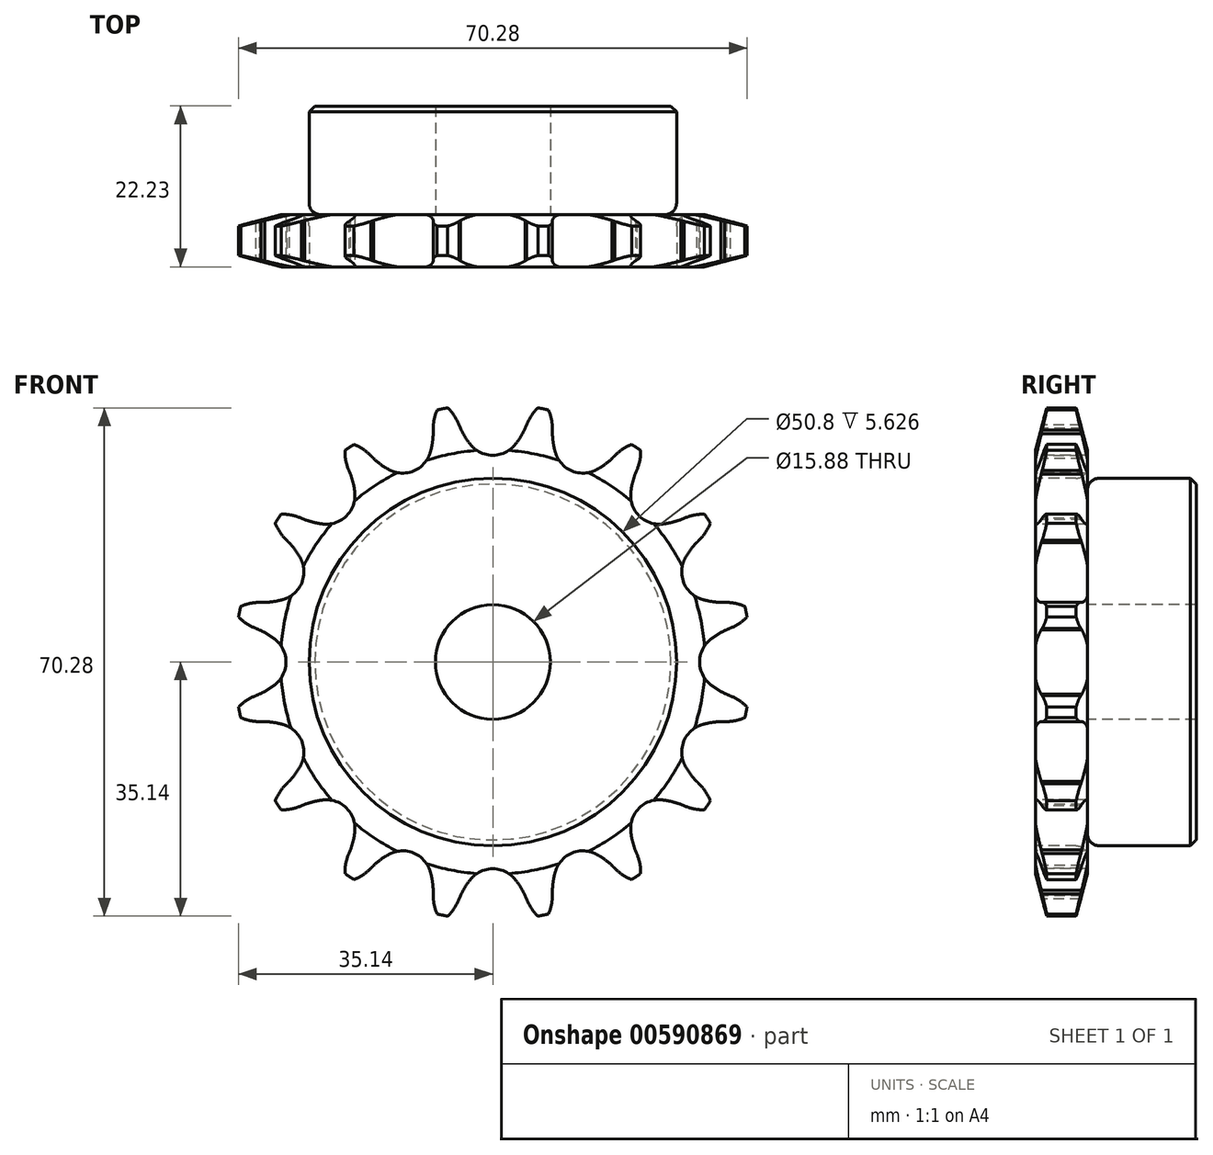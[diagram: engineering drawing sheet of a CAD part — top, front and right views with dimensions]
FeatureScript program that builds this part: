
annotation { "Feature Type Name" : "Feature", "Feature Type Description" : "" }
export const myFeature = defineFeature(function(context is Context, id is Id, definition is map)
    precondition{}
    {
        {
            var Q0;
            Q0=qCreatedBy(makeId("Right.planeOp"),FACE);
            var sketch = newSketch(context, id + "F0", { "sketchPlane" : qUnion([Q0])});
            skLineSegment(sketch, "E0", {"start": v(0, 0) * mm, "end": v(16.36, 0) * mm, "construction": true});
            skLineSegment(sketch, "E1.bottom", {"start": v(0, 7.94) * mm, "end": v(7.21, 7.94) * mm});
            skLineSegment(sketch, "E1.top", {"start": v(0, 35.69) * mm, "end": v(7.21, 35.69) * mm});
            skLineSegment(sketch, "E1.left", {"start": v(0, 7.94) * mm, "end": v(0, 35.69) * mm});
            skLineSegment(sketch, "E1.right", {"start": v(7.21, 7.94) * mm, "end": v(7.21, 35.69) * mm});
            skLineSegment(sketch, "E2.bottom", {"start": v(0, 7.94) * mm, "end": v(22.23, 7.94) * mm});
            skLineSegment(sketch, "E2.top", {"start": v(0, 25.4) * mm, "end": v(22.23, 25.4) * mm});
            skLineSegment(sketch, "E2.left", {"start": v(0, 7.94) * mm, "end": v(0, 25.4) * mm});
            skLineSegment(sketch, "E2.right", {"start": v(22.23, 7.94) * mm, "end": v(22.22, 25.4) * mm});
            skLineSegment(sketch, "E3.MirrorCS", {"start": v(0, -7.94) * mm, "end": v(7.21, -7.94) * mm});
            skLineSegment(sketch, "E4.MirrorCS", {"start": v(22.23, -7.94) * mm, "end": v(22.23, -25.4) * mm});
            skLineSegment(sketch, "E5.MirrorCS", {"start": v(0, -7.94) * mm, "end": v(0, -25.4) * mm});
            skLineSegment(sketch, "E6.MirrorCS", {"start": v(0, -35.69) * mm, "end": v(7.21, -35.69) * mm});
            skLineSegment(sketch, "E7.MirrorCS", {"start": v(0, -7.94) * mm, "end": v(0, -35.69) * mm});
            skLineSegment(sketch, "E8.MirrorCS", {"start": v(7.21, -7.94) * mm, "end": v(7.21, -35.69) * mm});
            skLineSegment(sketch, "E9.MirrorCS", {"start": v(0, -7.94) * mm, "end": v(22.23, -7.94) * mm});
            skLineSegment(sketch, "E10.MirrorCS", {"start": v(0, -25.4) * mm, "end": v(22.23, -25.4) * mm});
            skSolve(sketch);
        }
        {
            var Q0;
            {var subQ5=sQuery(id+"F0.wireOp",EDGE,"E2.right");Q0=makeQuery(id+"F0.imprint","IMPRINT",FACE,{"disambiguationData":[TD([[makeQuery(id+"F0.imprint","IMPRINT",EDGE,{"derivedFrom":subQ5}),1.0]])]});}
            var Q1;
            {var subQ5=sQuery(id+"F0.wireOp",EDGE,"E2.left");Q1=makeQuery(id+"F0.imprint","IMPRINT",FACE,{"disambiguationData":[TD([[makeQuery(id+"F0.imprint","IMPRINT",EDGE,{"derivedFrom":subQ5}),-1.0]])]});}
            var Q2;
            {var subQ0=sQuery(id+"F0.wireOp",EDGE,"E1.top");Q2=makeQuery(id+"F0.imprint","IMPRINT",FACE,{"disambiguationData":[TD([[makeQuery(id+"F0.imprint","IMPRINT",EDGE,{"derivedFrom":subQ0}),-1.0]])]});}
            var Q3;
            Q3=sQuery(id+"F0.wireOp",EDGE,"E0");
            revolve(context, id + "F1", {"entities" : qUnion([Q0, Q1, Q2]), "axis" : qUnion([Q3]), "revolveType" : RevolveType.FULL});
        }
        {
            var Q0;
            Q0=makeQuery(id+"F1.opRevolve","SWEPT_EDGE",EDGE,{"disambiguationData":[OSD([sQuery(id+"F0.wireOp",EDGE,"E1.right"),sQuery(id+"F0.wireOp",EDGE,"E2.top")])]});
            fillet(context, id + "F2", {"entities" : qUnion([Q0]), "radius" : 1.59 * mm, "tangentPropagation" : true, "allowEdgeOverflow" : false});
        }
        {
            var Q0;
            Q0=makeQuery(id+"F1.opRevolve","SWEPT_EDGE",EDGE,{"disambiguationData":[OSD([sQuery(id+"F0.wireOp",EDGE,"E2.top"),sQuery(id+"F0.wireOp",EDGE,"E2.right")])]});
            chamfer(context, id + "F3", {"entities" : qUnion([Q0]), "width" : 0.8 * mm, "tangentPropagation" : true});
        }
        {
            var Q0;
            Q0=makeQuery(id+"F1.opRevolve","SWEPT_EDGE",EDGE,{"disambiguationData":[OSD([sQuery(id+"F0.wireOp",EDGE,"E1.top"),sQuery(id+"F0.wireOp",EDGE,"E1.left")])]});
            var Q1;
            Q1=makeQuery(id+"F1.opRevolve","SWEPT_EDGE",EDGE,{"disambiguationData":[OSD([sQuery(id+"F0.wireOp",EDGE,"E1.top"),sQuery(id+"F0.wireOp",EDGE,"E1.right")])]});
            chamfer(context, id + "F4", {"entities" : qUnion([Q0, Q1]), "chamferType" : ChamferType.TWO_OFFSETS, "width1" : 6.35 * mm, "oppositeDirection" : false, "width2" : 1.57 * mm, "tangentPropagation" : true});
        }
        {
            var Q0;
            Q0=makeQuery(id+"F1.opRevolve","SWEPT_FACE",FACE,{"disambiguationData":[OSD([sQuery(id+"F0.wireOp",EDGE,"E1.left"),sQuery(id+"F0.wireOp",EDGE,"E2.left")])]});
            var sketch = newSketch(context, id + "F5", { "sketchPlane" : qUnion([Q0])});
            skCircle(sketch, "E11", {"center": v(0, 0) * mm, "radius": 32.55 * mm, "construction": true});
            skLineSegment(sketch, "E12", {"start": v(0, 0) * mm, "end": v(0, 32.55) * mm, "construction": true});
            skLineSegment(sketch, "E13", {"start": v(0, 32.55) * mm, "end": v(42.53, 32.55) * mm, "construction": true});
            skLineSegment(sketch, "E14", {"start": v(0, 32.55) * mm, "end": v(5, 36.56) * mm, "construction": true});
            skLineSegment(sketch, "E15", {"start": v(5, 36.56) * mm, "end": v(-4.46, 32.3) * mm, "construction": true});
            skLineSegment(sketch, "E16", {"start": v(0, 0) * mm, "end": v(-7.13, 35.87) * mm, "construction": true});
            skArc(sketch, "E17", {"start": v(-7.13, 35.87) * mm, "mid": v(-15.95, 26.27) * mm, "end": v(-4.65, 32.77) * mm, "construction": true});
            skArc(sketch, "E18", {"start": v(-4.65, 32.77) * mm, "mid": v(-5.66, 34.5) * mm, "end": v(-7.13, 35.87) * mm});
            skCircle(sketch, "E19.MirrorC", {"center": v(-5, 36.56) * mm, "radius": 10.36 * mm, "construction": true});
            skArc(sketch, "E20.MirrorCS", {"start": v(7.13, 35.87) * mm, "mid": v(15.95, 26.27) * mm, "end": v(4.65, 32.77) * mm, "construction": true});
            skLineSegment(sketch, "E21", {"start": v(-4.65, 32.77) * mm, "end": v(-4.65, 32.77) * mm});
            skLineSegment(sketch, "E22", {"start": v(-4.65, 32.77) * mm, "end": v(-6.37, 36.55) * mm, "construction": true});
            skArc(sketch, "E23", {"start": v(-4.46, 32.3) * mm, "mid": v(-3.84, 31.14) * mm, "end": v(-3.1, 30.07) * mm});
            skArc(sketch, "E24", {"start": v(-3.1, 30.07) * mm, "mid": v(13.83, 41.97) * mm, "end": v(-4.46, 32.3) * mm, "construction": true});
            skArc(sketch, "E25.MirrorCS", {"start": v(4.46, 32.3) * mm, "mid": v(3.84, 31.14) * mm, "end": v(3.1, 30.07) * mm});
            skLineSegment(sketch, "E26.MirrorCS", {"start": v(4.46, 32.3) * mm, "end": v(4.65, 32.77) * mm});
            skArc(sketch, "E27.MirrorCS", {"start": v(4.65, 32.77) * mm, "mid": v(5.66, 34.5) * mm, "end": v(7.13, 35.87) * mm});
            skLineSegment(sketch, "E28", {"start": v(-3.1, 30.07) * mm, "end": v(-3.1, 30.07) * mm});
            skArc(sketch, "E29", {"start": v(-3.1, 30.07) * mm, "mid": v(0, 28.59) * mm, "end": v(3.1, 30.07) * mm});
            skArc(sketch, "E30", {"start": v(3.1, 30.07) * mm, "mid": v(0, 36.51) * mm, "end": v(-3.1, 30.07) * mm, "construction": true});
            skLineSegment(sketch, "E31", {"start": v(-4.65, 32.77) * mm, "end": v(-4.46, 32.3) * mm});
            skArc(sketch, "E32.1.0", {"start": v(-16.84, 28.5) * mm, "mid": v(-18.43, 29.72) * mm, "end": v(-20.32, 30.4) * mm});
            skLineSegment(sketch, "E32.1.1", {"start": v(-16.84, 28.5) * mm, "end": v(-16.48, 28.14) * mm});
            skArc(sketch, "E32.1.2", {"start": v(-16.48, 28.14) * mm, "mid": v(-15.47, 27.3) * mm, "end": v(-14.36, 26.6) * mm});
            skArc(sketch, "E32.1.3", {"start": v(-14.36, 26.6) * mm, "mid": v(-10.94, 26.41) * mm, "end": v(-8.65, 28.96) * mm});
            skArc(sketch, "E32.1.4", {"start": v(-8.24, 31.55) * mm, "mid": v(-8.37, 30.24) * mm, "end": v(-8.65, 28.96) * mm});
            skLineSegment(sketch, "E32.1.5", {"start": v(-8.24, 31.55) * mm, "end": v(-8.24, 32.06) * mm});
            skArc(sketch, "E32.1.6", {"start": v(-8.24, 32.06) * mm, "mid": v(-7.98, 34.05) * mm, "end": v(-7.13, 35.87) * mm});
            skArc(sketch, "E32.2.0", {"start": v(-26.46, 19.88) * mm, "mid": v(-28.4, 20.4) * mm, "end": v(-30.4, 20.32) * mm});
            skLineSegment(sketch, "E32.2.1", {"start": v(-26.46, 19.88) * mm, "end": v(-26, 19.69) * mm});
            skArc(sketch, "E32.2.2", {"start": v(-26, 19.69) * mm, "mid": v(-24.74, 19.3) * mm, "end": v(-23.45, 19.08) * mm});
            skArc(sketch, "E32.2.3", {"start": v(-23.45, 19.08) * mm, "mid": v(-20.21, 20.21) * mm, "end": v(-19.08, 23.45) * mm});
            skArc(sketch, "E32.2.4", {"start": v(-19.69, 26) * mm, "mid": v(-19.3, 24.74) * mm, "end": v(-19.08, 23.45) * mm});
            skLineSegment(sketch, "E32.2.5", {"start": v(-19.69, 26) * mm, "end": v(-19.88, 26.46) * mm});
            skArc(sketch, "E32.2.6", {"start": v(-19.88, 26.46) * mm, "mid": v(-20.4, 28.4) * mm, "end": v(-20.32, 30.4) * mm});
            skArc(sketch, "E33.1.3.0", {"start": v(-32.06, 8.24) * mm, "mid": v(-34.05, 7.98) * mm, "end": v(-35.87, 7.13) * mm});
            skLineSegment(sketch, "E33.4.3.0", {"start": v(-32.06, 8.24) * mm, "end": v(-31.55, 8.24) * mm});
            skArc(sketch, "E33.7.3.0", {"start": v(-31.55, 8.24) * mm, "mid": v(-30.24, 8.37) * mm, "end": v(-28.96, 8.65) * mm});
            skArc(sketch, "E33.11.3.0", {"start": v(-28.96, 8.65) * mm, "mid": v(-26.41, 10.94) * mm, "end": v(-26.6, 14.36) * mm});
            skArc(sketch, "E33.15.3.0", {"start": v(-28.14, 16.48) * mm, "mid": v(-27.3, 15.47) * mm, "end": v(-26.6, 14.36) * mm});
            skLineSegment(sketch, "E33.19.3.0", {"start": v(-28.14, 16.48) * mm, "end": v(-28.5, 16.84) * mm});
            skArc(sketch, "E33.22.3.0", {"start": v(-28.5, 16.84) * mm, "mid": v(-29.72, 18.43) * mm, "end": v(-30.4, 20.32) * mm});
            skArc(sketch, "E33.1.4.0", {"start": v(-32.77, -4.65) * mm, "mid": v(-34.5, -5.66) * mm, "end": v(-35.87, -7.13) * mm});
            skLineSegment(sketch, "E33.4.4.0", {"start": v(-32.77, -4.65) * mm, "end": v(-32.3, -4.46) * mm});
            skArc(sketch, "E33.7.4.0", {"start": v(-32.3, -4.46) * mm, "mid": v(-31.14, -3.84) * mm, "end": v(-30.07, -3.1) * mm});
            skArc(sketch, "E33.11.4.0", {"start": v(-30.07, -3.1) * mm, "mid": v(-28.59, 0) * mm, "end": v(-30.07, 3.1) * mm});
            skArc(sketch, "E33.15.4.0", {"start": v(-32.3, 4.46) * mm, "mid": v(-31.14, 3.84) * mm, "end": v(-30.07, 3.1) * mm});
            skLineSegment(sketch, "E33.19.4.0", {"start": v(-32.3, 4.46) * mm, "end": v(-32.77, 4.65) * mm});
            skArc(sketch, "E33.22.4.0", {"start": v(-32.77, 4.65) * mm, "mid": v(-34.5, 5.66) * mm, "end": v(-35.87, 7.13) * mm});
            skArc(sketch, "E33.1.5.0", {"start": v(-28.5, -16.84) * mm, "mid": v(-29.72, -18.43) * mm, "end": v(-30.4, -20.32) * mm});
            skLineSegment(sketch, "E33.4.5.0", {"start": v(-28.5, -16.84) * mm, "end": v(-28.14, -16.48) * mm});
            skArc(sketch, "E33.7.5.0", {"start": v(-28.14, -16.48) * mm, "mid": v(-27.3, -15.47) * mm, "end": v(-26.6, -14.36) * mm});
            skArc(sketch, "E33.11.5.0", {"start": v(-26.6, -14.36) * mm, "mid": v(-26.41, -10.94) * mm, "end": v(-28.96, -8.65) * mm});
            skArc(sketch, "E33.15.5.0", {"start": v(-31.55, -8.24) * mm, "mid": v(-30.24, -8.37) * mm, "end": v(-28.96, -8.65) * mm});
            skLineSegment(sketch, "E33.19.5.0", {"start": v(-31.55, -8.24) * mm, "end": v(-32.06, -8.24) * mm});
            skArc(sketch, "E33.22.5.0", {"start": v(-32.06, -8.24) * mm, "mid": v(-34.05, -7.98) * mm, "end": v(-35.87, -7.13) * mm});
            skArc(sketch, "E33.1.6.0", {"start": v(-19.88, -26.46) * mm, "mid": v(-20.4, -28.4) * mm, "end": v(-20.32, -30.4) * mm});
            skLineSegment(sketch, "E33.4.6.0", {"start": v(-19.88, -26.46) * mm, "end": v(-19.69, -26) * mm});
            skArc(sketch, "E33.7.6.0", {"start": v(-19.69, -26) * mm, "mid": v(-19.3, -24.74) * mm, "end": v(-19.08, -23.45) * mm});
            skArc(sketch, "E33.11.6.0", {"start": v(-19.08, -23.45) * mm, "mid": v(-20.21, -20.21) * mm, "end": v(-23.45, -19.08) * mm});
            skArc(sketch, "E33.15.6.0", {"start": v(-26, -19.69) * mm, "mid": v(-24.74, -19.3) * mm, "end": v(-23.45, -19.08) * mm});
            skLineSegment(sketch, "E33.19.6.0", {"start": v(-26, -19.69) * mm, "end": v(-26.46, -19.88) * mm});
            skArc(sketch, "E33.22.6.0", {"start": v(-26.46, -19.88) * mm, "mid": v(-28.4, -20.4) * mm, "end": v(-30.4, -20.32) * mm});
            skArc(sketch, "E33.1.7.0", {"start": v(-8.24, -32.06) * mm, "mid": v(-7.98, -34.05) * mm, "end": v(-7.13, -35.87) * mm});
            skLineSegment(sketch, "E33.4.7.0", {"start": v(-8.24, -32.06) * mm, "end": v(-8.24, -31.55) * mm});
            skArc(sketch, "E33.7.7.0", {"start": v(-8.24, -31.55) * mm, "mid": v(-8.37, -30.24) * mm, "end": v(-8.65, -28.96) * mm});
            skArc(sketch, "E33.11.7.0", {"start": v(-8.65, -28.96) * mm, "mid": v(-10.94, -26.41) * mm, "end": v(-14.36, -26.6) * mm});
            skArc(sketch, "E33.15.7.0", {"start": v(-16.48, -28.14) * mm, "mid": v(-15.47, -27.3) * mm, "end": v(-14.36, -26.6) * mm});
            skLineSegment(sketch, "E33.19.7.0", {"start": v(-16.48, -28.14) * mm, "end": v(-16.84, -28.5) * mm});
            skArc(sketch, "E33.22.7.0", {"start": v(-16.84, -28.5) * mm, "mid": v(-18.43, -29.72) * mm, "end": v(-20.32, -30.4) * mm});
            skArc(sketch, "E33.1.8.0", {"start": v(4.65, -32.77) * mm, "mid": v(5.66, -34.5) * mm, "end": v(7.13, -35.87) * mm});
            skLineSegment(sketch, "E33.4.8.0", {"start": v(4.65, -32.77) * mm, "end": v(4.46, -32.3) * mm});
            skArc(sketch, "E33.7.8.0", {"start": v(4.46, -32.3) * mm, "mid": v(3.84, -31.14) * mm, "end": v(3.1, -30.07) * mm});
            skArc(sketch, "E33.11.8.0", {"start": v(3.1, -30.07) * mm, "mid": v(0, -28.59) * mm, "end": v(-3.1, -30.07) * mm});
            skArc(sketch, "E33.15.8.0", {"start": v(-4.46, -32.3) * mm, "mid": v(-3.84, -31.14) * mm, "end": v(-3.1, -30.07) * mm});
            skLineSegment(sketch, "E33.19.8.0", {"start": v(-4.46, -32.3) * mm, "end": v(-4.65, -32.77) * mm});
            skArc(sketch, "E33.22.8.0", {"start": v(-4.65, -32.77) * mm, "mid": v(-5.66, -34.5) * mm, "end": v(-7.13, -35.87) * mm});
            skArc(sketch, "E33.1.9.0", {"start": v(16.84, -28.5) * mm, "mid": v(18.43, -29.72) * mm, "end": v(20.32, -30.4) * mm});
            skLineSegment(sketch, "E33.4.9.0", {"start": v(16.84, -28.5) * mm, "end": v(16.48, -28.14) * mm});
            skArc(sketch, "E33.7.9.0", {"start": v(16.48, -28.14) * mm, "mid": v(15.47, -27.3) * mm, "end": v(14.36, -26.6) * mm});
            skArc(sketch, "E33.11.9.0", {"start": v(14.36, -26.6) * mm, "mid": v(10.94, -26.41) * mm, "end": v(8.65, -28.96) * mm});
            skArc(sketch, "E33.15.9.0", {"start": v(8.24, -31.55) * mm, "mid": v(8.37, -30.24) * mm, "end": v(8.65, -28.96) * mm});
            skLineSegment(sketch, "E33.19.9.0", {"start": v(8.24, -31.55) * mm, "end": v(8.24, -32.06) * mm});
            skArc(sketch, "E33.22.9.0", {"start": v(8.24, -32.06) * mm, "mid": v(7.98, -34.05) * mm, "end": v(7.13, -35.87) * mm});
            skArc(sketch, "E33.1.10.0", {"start": v(26.46, -19.88) * mm, "mid": v(28.4, -20.4) * mm, "end": v(30.4, -20.32) * mm});
            skLineSegment(sketch, "E33.4.10.0", {"start": v(26.46, -19.88) * mm, "end": v(26, -19.69) * mm});
            skArc(sketch, "E33.7.10.0", {"start": v(26, -19.69) * mm, "mid": v(24.74, -19.3) * mm, "end": v(23.45, -19.08) * mm});
            skArc(sketch, "E33.11.10.0", {"start": v(23.45, -19.08) * mm, "mid": v(20.21, -20.21) * mm, "end": v(19.08, -23.45) * mm});
            skArc(sketch, "E33.15.10.0", {"start": v(19.69, -26) * mm, "mid": v(19.3, -24.74) * mm, "end": v(19.08, -23.45) * mm});
            skLineSegment(sketch, "E33.19.10.0", {"start": v(19.69, -26) * mm, "end": v(19.88, -26.46) * mm});
            skArc(sketch, "E33.22.10.0", {"start": v(19.88, -26.46) * mm, "mid": v(20.4, -28.4) * mm, "end": v(20.32, -30.4) * mm});
            skArc(sketch, "E33.1.11.0", {"start": v(32.06, -8.24) * mm, "mid": v(34.05, -7.98) * mm, "end": v(35.87, -7.13) * mm});
            skLineSegment(sketch, "E33.4.11.0", {"start": v(32.06, -8.24) * mm, "end": v(31.55, -8.24) * mm});
            skArc(sketch, "E33.7.11.0", {"start": v(31.55, -8.24) * mm, "mid": v(30.24, -8.37) * mm, "end": v(28.96, -8.65) * mm});
            skArc(sketch, "E33.11.11.0", {"start": v(28.96, -8.65) * mm, "mid": v(26.41, -10.94) * mm, "end": v(26.6, -14.36) * mm});
            skArc(sketch, "E33.15.11.0", {"start": v(28.14, -16.48) * mm, "mid": v(27.3, -15.47) * mm, "end": v(26.6, -14.36) * mm});
            skLineSegment(sketch, "E33.19.11.0", {"start": v(28.14, -16.48) * mm, "end": v(28.5, -16.84) * mm});
            skArc(sketch, "E33.22.11.0", {"start": v(28.5, -16.84) * mm, "mid": v(29.72, -18.43) * mm, "end": v(30.4, -20.32) * mm});
            skArc(sketch, "E33.1.12.0", {"start": v(32.77, 4.65) * mm, "mid": v(34.5, 5.66) * mm, "end": v(35.87, 7.13) * mm});
            skLineSegment(sketch, "E33.4.12.0", {"start": v(32.77, 4.65) * mm, "end": v(32.3, 4.46) * mm});
            skArc(sketch, "E33.7.12.0", {"start": v(32.3, 4.46) * mm, "mid": v(31.14, 3.84) * mm, "end": v(30.07, 3.1) * mm});
            skArc(sketch, "E33.11.12.0", {"start": v(30.07, 3.1) * mm, "mid": v(28.59, 0) * mm, "end": v(30.07, -3.1) * mm});
            skArc(sketch, "E33.15.12.0", {"start": v(32.3, -4.46) * mm, "mid": v(31.14, -3.84) * mm, "end": v(30.07, -3.1) * mm});
            skLineSegment(sketch, "E33.19.12.0", {"start": v(32.3, -4.46) * mm, "end": v(32.77, -4.65) * mm});
            skArc(sketch, "E33.22.12.0", {"start": v(32.77, -4.65) * mm, "mid": v(34.5, -5.66) * mm, "end": v(35.87, -7.13) * mm});
            skArc(sketch, "E33.1.13.0", {"start": v(28.5, 16.84) * mm, "mid": v(29.72, 18.43) * mm, "end": v(30.4, 20.32) * mm});
            skLineSegment(sketch, "E33.4.13.0", {"start": v(28.5, 16.84) * mm, "end": v(28.14, 16.48) * mm});
            skArc(sketch, "E33.7.13.0", {"start": v(28.14, 16.48) * mm, "mid": v(27.3, 15.47) * mm, "end": v(26.6, 14.36) * mm});
            skArc(sketch, "E33.11.13.0", {"start": v(26.6, 14.36) * mm, "mid": v(26.41, 10.94) * mm, "end": v(28.96, 8.65) * mm});
            skArc(sketch, "E33.15.13.0", {"start": v(31.55, 8.24) * mm, "mid": v(30.24, 8.37) * mm, "end": v(28.96, 8.65) * mm});
            skLineSegment(sketch, "E33.19.13.0", {"start": v(31.55, 8.24) * mm, "end": v(32.06, 8.24) * mm});
            skArc(sketch, "E33.22.13.0", {"start": v(32.06, 8.24) * mm, "mid": v(34.05, 7.98) * mm, "end": v(35.87, 7.13) * mm});
            skArc(sketch, "E33.1.14.0", {"start": v(19.88, 26.46) * mm, "mid": v(20.4, 28.4) * mm, "end": v(20.32, 30.4) * mm});
            skLineSegment(sketch, "E33.4.14.0", {"start": v(19.88, 26.46) * mm, "end": v(19.69, 26) * mm});
            skArc(sketch, "E33.7.14.0", {"start": v(19.69, 26) * mm, "mid": v(19.3, 24.74) * mm, "end": v(19.08, 23.45) * mm});
            skArc(sketch, "E33.11.14.0", {"start": v(19.08, 23.45) * mm, "mid": v(20.21, 20.21) * mm, "end": v(23.45, 19.08) * mm});
            skArc(sketch, "E33.15.14.0", {"start": v(26, 19.69) * mm, "mid": v(24.74, 19.3) * mm, "end": v(23.45, 19.08) * mm});
            skLineSegment(sketch, "E33.19.14.0", {"start": v(26, 19.69) * mm, "end": v(26.46, 19.88) * mm});
            skArc(sketch, "E33.22.14.0", {"start": v(26.46, 19.88) * mm, "mid": v(28.4, 20.4) * mm, "end": v(30.4, 20.32) * mm});
            skArc(sketch, "E33.1.15.0", {"start": v(8.24, 32.06) * mm, "mid": v(7.98, 34.05) * mm, "end": v(7.13, 35.87) * mm});
            skLineSegment(sketch, "E33.4.15.0", {"start": v(8.24, 32.06) * mm, "end": v(8.24, 31.55) * mm});
            skArc(sketch, "E33.7.15.0", {"start": v(8.24, 31.55) * mm, "mid": v(8.37, 30.24) * mm, "end": v(8.65, 28.96) * mm});
            skArc(sketch, "E33.11.15.0", {"start": v(8.65, 28.96) * mm, "mid": v(10.94, 26.41) * mm, "end": v(14.36, 26.6) * mm});
            skArc(sketch, "E33.15.15.0", {"start": v(16.48, 28.14) * mm, "mid": v(15.47, 27.3) * mm, "end": v(14.36, 26.6) * mm});
            skLineSegment(sketch, "E33.19.15.0", {"start": v(16.48, 28.14) * mm, "end": v(16.84, 28.5) * mm});
            skArc(sketch, "E33.22.15.0", {"start": v(16.84, 28.5) * mm, "mid": v(18.43, 29.72) * mm, "end": v(20.32, 30.4) * mm});
            skSolve(sketch);
        }
        {
            var Q0;
            Q0 = qSketchRegion(id + "F5", true);
            extrude(context, id + "F6", {"entities" : qUnion([Q0]), "operationType" : NewBodyOperationType.INTERSECT, "endBound" : BoundingType.THROUGH_ALL, "oppositeDirection" : true, "depth" : 25.4 * mm, "offsetDistance" : 25.4 * mm});
        }
    });
